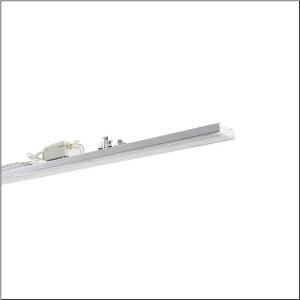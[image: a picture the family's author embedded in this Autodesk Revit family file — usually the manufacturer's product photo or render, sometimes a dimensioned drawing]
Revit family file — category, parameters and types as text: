
# Revit family: licross_r__11_recessed_mo_51tl12dn4axg3s_f752
name_source: partatom
category: Lighting Fixtures
units: mm (PartAtom-declared; Revit-internal decimal feet)

## family parameters
Cut with Voids When Loaded = No
Host = Face
Light Source = No
Part Type = Normal
Room Calculation Point = No
Round Connector Dimension = Use Diameter
Shared = No

## types (1)
- --- (1 x LED, 1010 lm, 6.7 W, 4000K)
    Apparent Load = 7 VA
    CIE Flux Codes = 67 92 99 100 100
    Color Rendering = 80
    Color Temperature = 4000K
    Default Elevation = 1800 mm
    Description = Licross® 11 Recessed MO, luminaire insert, of sheet steel, coil coated, white, length: 1.500mm, width: 66mm, height: 67mm, LED rated luminous flux: 10.240lm, light colour: 840, SDCM (Standard Deviation of Colour Matching)MacAdam ≤ 2 SDCM (initial), control gear: DALI 2 (for two DALI lines), with plug, 6-pole, with phase selection, for trunking rail, 14-core, mains connection: 220..240V, AC, 50/60Hz, rated input power: 61W, for trunking rail, 14-core, internal wiring halogen-free, for emergency light function, converter,control gear: single battery element, battery: LiFePO4, 9Ah, primary optical cover: cover, of PMMA, light emission: direct distribution, primary light characteristic: symmetric, protection rating (complete): IP40, insulation class (complete): insulation class I (protective earthing), certification: CE, UKCA, protection symbol: D if used in an environment without relevant dust loads with corresponding accessories, impact resistance: IK06, permissible ambient temperature for indoor applications: +5..+35°C, standard: EN 60598-2-22, LABS conformity tested according to VDMA 24364:2018-05, reducing of maximum allowable ambient temperature of 5°C with ceiling mounting, corresponds to IFS (International Featured Standards) requirements for safety and quality in the food industry, packaging unit: 1 piece
    Height = 58 mm
    Lamp = 1 x LED
    Lamp Light Flux = 1010 lm
    Lamp Power = 6.7 W
    Lamp count = 1
    Length = 1500 mm
    Luminous efficacy = 151 lm/W
    Manufacturer = Siteco
    ModVariant = No
    Model = 51TL12DN4AXG3S
    Mounting Place = Ceiling
    Mounting Type = Pendant
    Number of Poles = 1
    OnlyDefault = Yes
    Power Factor = 1
    Product Name = Licross® 11 Recessed MO
    Product group = luminaire insert | ceiling pendant
    ProductGroupID = 901
    Protection Class = Protection class I
    Protection Degree = IP 40
    RLX_Detail_Level = 1
    RLX_Emergency_Light_Flux = 0 lm
    RLX_Emergency_Type = 0
    RLX_Emergency_Type_DB = No
    RlxData = <blob elided: 24881 chars, md5=7041918a>
    Socket = socket
    Standby Power = 0 W
    System Light Flux = 1010 lm
    System Power = 7 W
    Type Comments = : emergency light operation: 3 h
    Type Image = l_1296930.jpg
    URL = http://relux.com
    VarID = @adj_098109
    Voltage = 0 V
    Weight = 0.00 kg
    Width = 66 mm

## geometry (parser evidence)
native form markers: Blend x4, Sweep x10
no freeform markers — native parametric forms only
